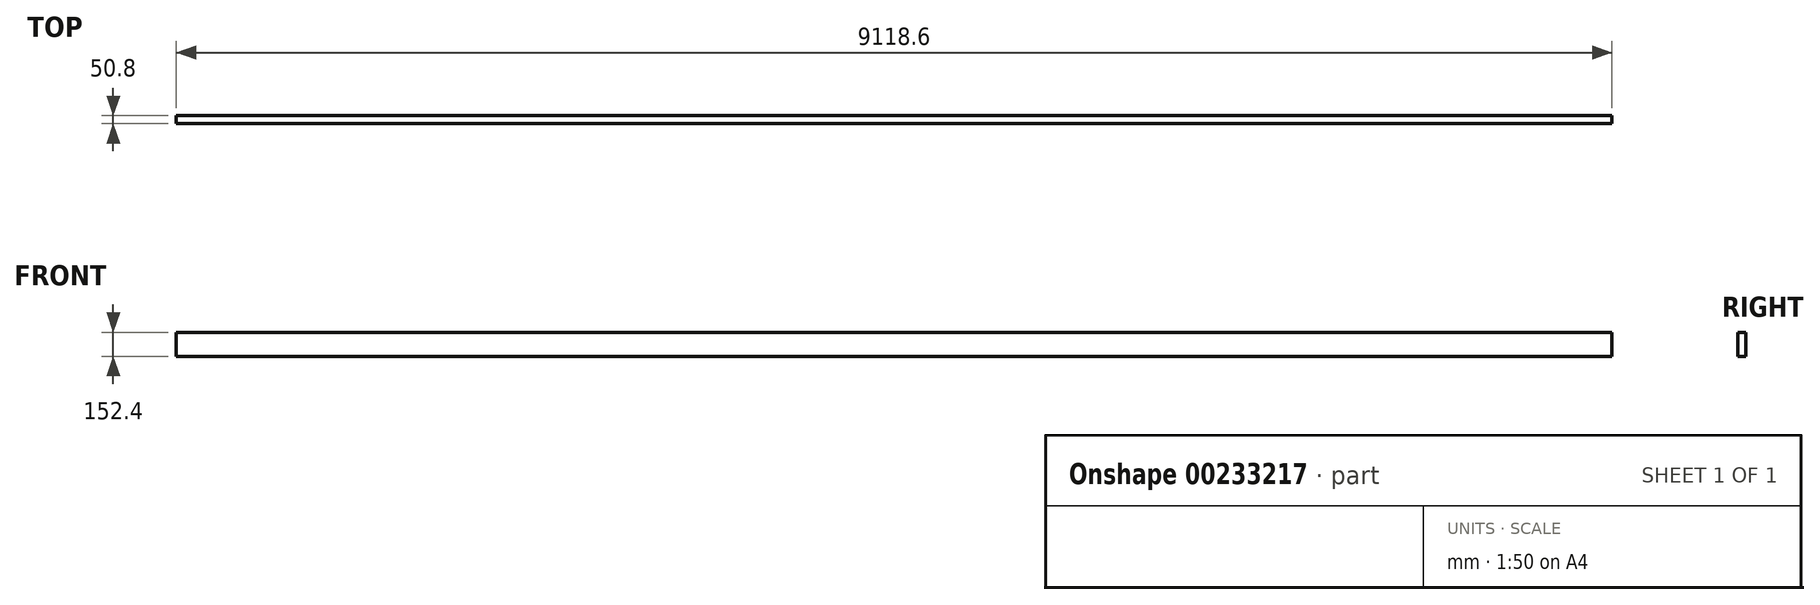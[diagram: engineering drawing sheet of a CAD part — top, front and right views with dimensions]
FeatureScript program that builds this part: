
annotation { "Feature Type Name" : "Feature", "Feature Type Description" : "" }
export const myFeature = defineFeature(function(context is Context, id is Id, definition is map)
    precondition{}
    {
        {
            var Q0;
            Q0=qCreatedBy(makeId("Front.planeOp"),FACE);
            var sketch = newSketch(context, id + "F0", { "sketchPlane" : qUnion([Q0])});
            skLineSegment(sketch, "E0.bottom", {"start": v(-4575.8, -1653.69) * mm, "end": v(4542.8, -1653.69) * mm});
            skLineSegment(sketch, "E0.top", {"start": v(-4575.8, -1806.09) * mm, "end": v(4542.8, -1806.09) * mm});
            skLineSegment(sketch, "E0.left", {"start": v(-4575.8, -1653.69) * mm, "end": v(-4575.8, -1806.09) * mm});
            skLineSegment(sketch, "E0.right", {"start": v(4542.8, -1653.69) * mm, "end": v(4542.8, -1806.09) * mm});
            skSolve(sketch);
        }
        {
            var Q0;
            Q0 = qSketchRegion(id + "F0", true);
            extrude(context, id + "F1", {"entities" : qUnion([Q0]), "depth" : 50.8 * mm});
        }
    });
